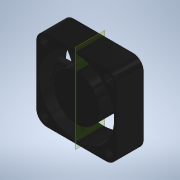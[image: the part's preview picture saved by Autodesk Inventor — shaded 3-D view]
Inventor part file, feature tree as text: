
AUTODESK INVENTOR PART (.ipt)
format: ipt  version: 2020 (Build 240168000, 168)  size: 438,272 bytes
history: native  units: mm
features: plane x1, other x1
ambient origin geometry x8: Origin, YZ Plane, XZ Plane, XY Plane, X Axis, Y Axis, Z Axis, Center Point
bodies: Solid1 (feature_tree)
feature tree (2):
  plane  "Work Plane1"
  other  "3010 fan"
